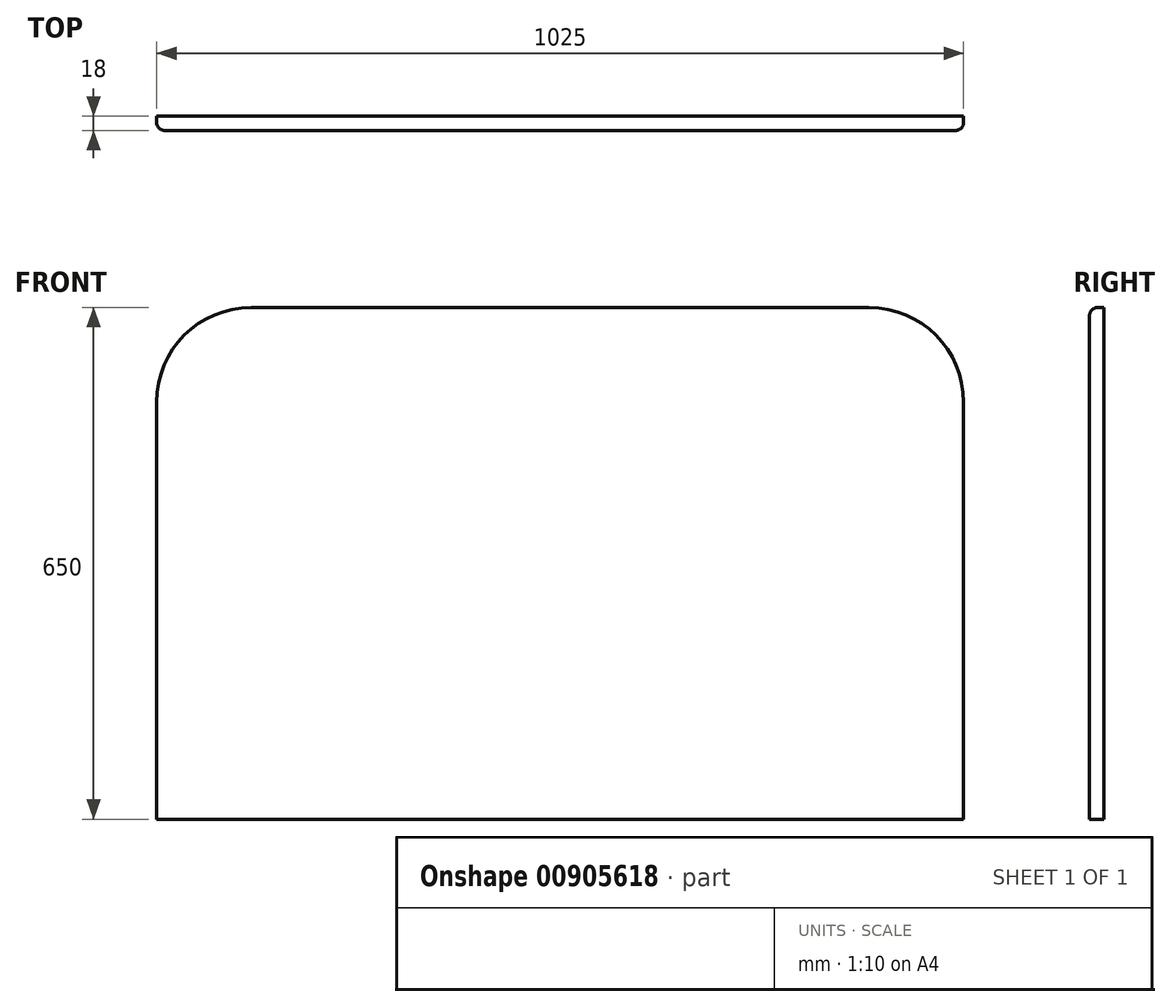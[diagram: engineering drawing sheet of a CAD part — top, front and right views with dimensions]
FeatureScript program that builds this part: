
annotation { "Feature Type Name" : "Feature", "Feature Type Description" : "" }
export const myFeature = defineFeature(function(context is Context, id is Id, definition is map)
    precondition{}
    {
        {
            var Q0;
            Q0=qCreatedBy(makeId("Front.planeOp"),FACE);
            var sketch = newSketch(context, id + "F0", { "sketchPlane" : qUnion([Q0])});
            skLineSegment(sketch, "E0.bottom", {"start": v(392.5, 325) * mm, "end": v(-392.5, 325) * mm});
            skLineSegment(sketch, "E0.top", {"start": v(512.5, -325) * mm, "end": v(-512.5, -325) * mm});
            skLineSegment(sketch, "E0.left", {"start": v(512.5, 205) * mm, "end": v(512.5, -325) * mm});
            skLineSegment(sketch, "E0.right", {"start": v(-512.5, 205) * mm, "end": v(-512.5, -325) * mm});
            skPoint(sketch, "E0.middle", {"position": v(0, 0) * mm});
            skPoint(sketch, "E1.visualSharp", {"position": v(-512.5, 325) * mm});
            skArc(sketch, "E1.filletArc", {"start": v(-392.5, 325) * mm, "mid": v(-477.35, 289.85) * mm, "end": v(-512.5, 205) * mm});
            skPoint(sketch, "E2.visualSharp", {"position": v(512.5, 325) * mm});
            skArc(sketch, "E2.filletArc", {"start": v(512.5, 205) * mm, "mid": v(477.35, 289.85) * mm, "end": v(392.5, 325) * mm});
            skSolve(sketch);
        }
        {
            var Q0;
            Q0=makeQuery(id+"F0.imprint","IMPRINT",FACE,{"disambiguationData":[TD([[makeQuery(id+"F0.imprint","IMPRINT",EDGE,{"derivedFrom":sQuery(id+"F0.wireOp",EDGE,"E0.bottom")}),1.0]])]});
            extrude(context, id + "F1", {"entities" : qUnion([Q0]), "depth" : 18 * mm, "offsetDistance" : 25 * mm});
        }
        {
            var Q0;
            Q0=makeQuery(id+"F1.opExtrude","CAP_EDGE",EDGE,{"disambiguationData":[OSD([sQuery(id+"F0.wireOp",EDGE,"E0.bottom")])],"isStart":false});
            fillet(context, id + "F2", {"entities" : qUnion([Q0]), "radius" : 10 * mm, "tangentPropagation" : true, "allowEdgeOverflow" : false});
        }
    });
